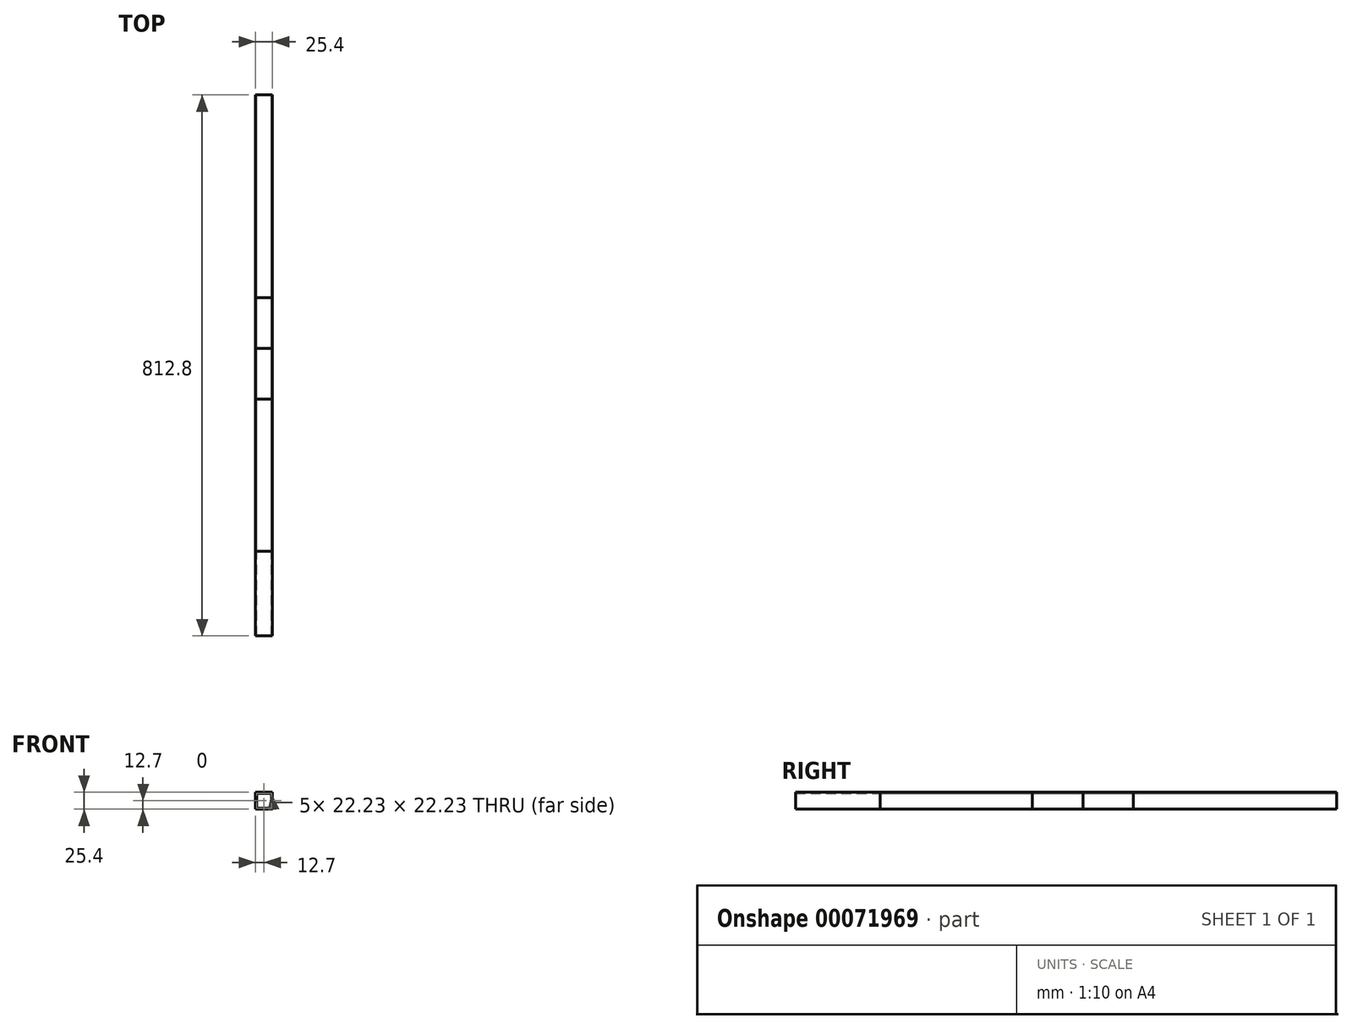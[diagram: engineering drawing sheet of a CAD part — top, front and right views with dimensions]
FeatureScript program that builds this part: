
annotation { "Feature Type Name" : "Feature", "Feature Type Description" : "" }
export const myFeature = defineFeature(function(context is Context, id is Id, definition is map)
    precondition{}
    {
        {
            var Q0;
            Q0=qCreatedBy(makeId("Front.planeOp"),FACE);
            var sketch = newSketch(context, id + "F0", { "sketchPlane" : qUnion([Q0])});
            skLineSegment(sketch, "E0.bottom", {"start": v(0, 0) * mm, "end": v(25.4, 0) * mm});
            skLineSegment(sketch, "E0.top", {"start": v(0, 25.4) * mm, "end": v(25.4, 25.4) * mm});
            skLineSegment(sketch, "E0.left", {"start": v(0, 0) * mm, "end": v(0, 25.4) * mm});
            skLineSegment(sketch, "E0.right", {"start": v(25.4, 0) * mm, "end": v(25.4, 25.4) * mm});
            skLineSegment(sketch, "E1.bottom", {"start": v(1.59, 1.59) * mm, "end": v(23.81, 1.59) * mm});
            skLineSegment(sketch, "E1.top", {"start": v(1.59, 23.81) * mm, "end": v(23.81, 23.81) * mm});
            skLineSegment(sketch, "E1.left", {"start": v(1.59, 1.59) * mm, "end": v(1.59, 23.81) * mm});
            skLineSegment(sketch, "E1.right", {"start": v(23.81, 1.59) * mm, "end": v(23.81, 23.81) * mm});
            skSolve(sketch);
        }
        {
            var Q0;
            Q0 = qSketchRegion(id + "F0", true);
            extrude(context, id + "F1", {"entities" : qUnion([Q0]), "depth" : 304.8 * mm});
        }
        {
            var Q0;
            Q0 = qSketchRegion(id + "F0", true);
            extrude(context, id + "F2", {"entities" : qUnion([Q0]), "depth" : 812.8 * mm});
        }
        {
            var Q0;
            Q0 = qSketchRegion(id + "F0", true);
            extrude(context, id + "F3", {"entities" : qUnion([Q0]), "depth" : 685.8 * mm});
        }
        {
            var Q0;
            Q0 = qSketchRegion(id + "F0", true);
            extrude(context, id + "F4", {"entities" : qUnion([Q0]), "depth" : 457.2 * mm});
        }
        {
            var Q0;
            Q0 = qSketchRegion(id + "F0", true);
            extrude(context, id + "F5", {"entities" : qUnion([Q0]), "depth" : 381 * mm});
        }
    });
